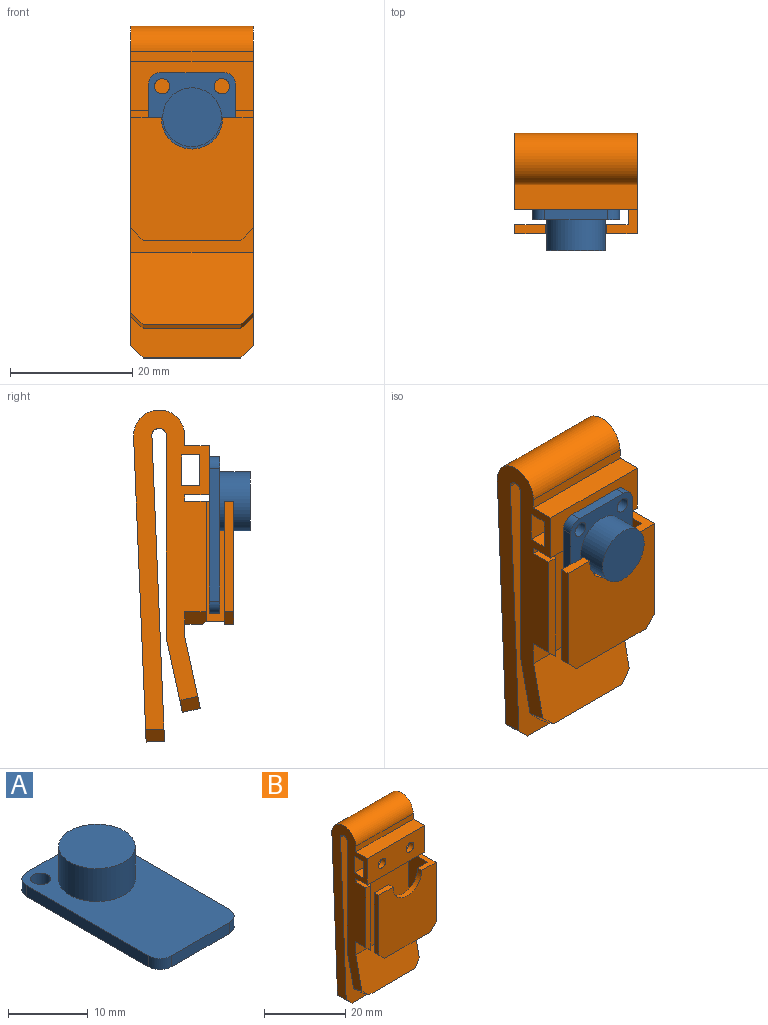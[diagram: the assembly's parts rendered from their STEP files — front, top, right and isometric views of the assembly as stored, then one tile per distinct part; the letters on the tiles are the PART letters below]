
ASSEMBLY  parts=2 mates=1
PART A: 14 faces, bbox 14.3x25.6x6.8 mm
  f0: plane 21.6x1.7mm, normal (1,0,0), area 36.7mm2, adj f1,f9,f10,f11
  f1: cylinder r=2mm len=2mm, axis (0,0,1), area 5.3mm2, adj f0,f2,f10,f11
  f2: plane 10.25x1.7mm, normal (0,1,0), area 17.4mm2, adj f1,f3,f10,f11
  f3: cylinder r=2mm len=2mm, axis (0,0,1), area 5.3mm2, adj f2,f4,f10,f11
  f4: plane 21.6x1.7mm, normal (-1,0,0), area 36.7mm2, adj f3,f5,f10,f11
  f5: cylinder r=2mm len=2mm, axis (0,0,1), area 5.3mm2, adj f4,f6,f10,f11
  f6: plane 10.25x1.7mm, normal (0,-1,0), area 17.4mm2, adj f5,f9,f10,f11
  f7: cylinder r=1.25mm len=2.5mm, axis (0,0,1), area 13.4mm2, adj f10,f11
  f8: cylinder r=1.25mm len=2.5mm, axis (0,0,1), area 13.4mm2, adj f10,f11
  f9: cylinder r=2mm len=2mm, axis (0,0,1), area 5.3mm2, adj f0,f6,f10,f11
  f10: plane 25.6x14.25mm, normal (0,0,-1), area 351.5mm2, adj f0,f1,f2,f3,f4,f5,f6,f7
  f11: plane 25.6x14.25mm, normal (0,0,1), area 279.2mm2, adj f0,f1,f2,f3,f4,f5,f6,f7
  f12: cylinder r=4.8mm len=9.6mm, axis (0,0,-1), area 152.3mm2, adj f11,f13
  f13: plane 9.6x9.6mm, normal (0,0,1), area 72.4mm2, adj f12
PART B: 43 faces, bbox 20x16.4x54.3 mm
  f0: cylinder r=1.35mm len=2.7mm, axis (0,-1,0), area 21.2mm2, adj f11,f40
  f1: cylinder r=1.35mm len=2.7mm, axis (0,-1,0), area 21.2mm2, adj f11,f40
  f2: plane 5x1.5mm, normal (0,0,1), area 7.5mm2, adj f3,f28,f31,f34
  f3: plane 18.04x1.5mm, normal (-1,0,0), area 27.1mm2, adj f2,f31,f34,f37
  f4: plane 16x1.5mm, normal (0,0,-1), area 24mm2, adj f31,f34,f37,f38
  f5: plane 4.59x3.5mm, normal (0,0,1), area 10.7mm2, adj f12,f16,f32,f35
  f6: plane 20x1.67mm, normal (0,-1,0), area 33.3mm2, adj f14,f16,f18,f26
  f7: plane 16x3mm, normal (0,-0.04,-1), area 48mm2, adj f9,f10,f21,f22
  f8: plane 16x2.93mm, normal (0,-0.21,-0.98), area 48mm2, adj f15,f17,f19,f20
  f9: plane 49.96x20mm, normal (0,-1,0.04), area 996.1mm2, adj f7,f13,f16,f18,f21,f22
  f10: plane 50.03x20mm, normal (0,1,-0.04), area 997.5mm2, adj f7,f14,f16,f18,f21,f22
  f11: plane 33.12x20mm, normal (0,1,0), area 651mm2, adj f0,f1,f13,f16,f17,f18
  f12: plane 23.13x20mm, normal (0,-1,0), area 344.4mm2, adj f5,f15,f16,f18,f25,f29,f30,f32
  f13: cylinder r=1.18mm len=20mm, axis (-1,0,0), area 73.6mm2, adj f9,f11,f16,f18
  f14: bspline ~20x8.36mm, area 263.2mm2, adj f6,f10,f16,f18
  f15: plane 20x11.77mm, normal (0,-0.98,0.21), area 237mm2, adj f8,f12,f16,f18,f19,f20
  f16: plane 52.25x12.37mm, normal (-1,0,0), area 378.9mm2, adj f5,f6,f9,f10,f11,f12,f13,f14
  f17: plane 20x12.09mm, normal (0,0.98,-0.21), area 243.5mm2, adj f8,f11,f16,f18,f19,f20
  f18: plane 52.25x16.37mm, normal (1,0,0), area 460.2mm2, adj f6,f9,f10,f11,f12,f13,f14,f15
  f19: plane 3.36x2.59mm, normal (0.71,-0.15,-0.69), area 8.5mm2, adj f8,f15,f17,f18
  f20: plane 3.36x2.59mm, normal (-0.71,-0.15,-0.69), area 8.5mm2, adj f8,f15,f16,f17
  f21: plane 3.08x2.12mm, normal (0.71,-0.03,-0.71), area 8.5mm2, adj f7,f9,f10,f18
  f22: plane 3.08x2.12mm, normal (-0.71,-0.03,-0.71), area 8.5mm2, adj f7,f9,f10,f16
  f23: cylinder r=1.35mm len=2.7mm, axis (0,-1,0), area 12.7mm2, adj f27,f39
  f24: cylinder r=1.35mm len=2.7mm, axis (0,-1,0), area 12.7mm2, adj f27,f39
  f25: plane 20x4mm, normal (0,0,-1), area 80mm2, adj f12,f16,f18,f27
  f26: plane 20x4mm, normal (0,0,1), area 80mm2, adj f6,f16,f18,f27
  f27: plane 20x8mm, normal (0,-1,0), area 148.5mm2, adj f16,f18,f23,f24,f25,f26
  f28: cylinder r=5mm len=10mm, axis (0,1,0), area 24mm2, adj f2,f30,f31,f34
  f29: plane 2.93x2.59mm, normal (0,0,-1), area 3.8mm2, adj f12,f32,f36
  f30: plane 8x5mm, normal (0,0,1), area 17.3mm2, adj f12,f18,f28,f31,f33,f34
  f31: plane 20.04x20mm, normal (0,-1,0), area 355.9mm2, adj f2,f3,f4,f18,f28,f30,f37,f38
  f32: plane 20.04x3.5mm, normal (0.75,-0.66,0), area 93.4mm2, adj f5,f12,f29,f35,f36
  f33: plane 19.54x6.5mm, normal (-1,0,0), area 127mm2, adj f12,f30,f34,f38
  f34: plane 20.04x18.5mm, normal (0,1,0), area 327.7mm2, adj f2,f3,f4,f28,f30,f33,f37,f38
  f35: plane 19.54x1.5mm, normal (0,-1,0), area 28.2mm2, adj f5,f16,f32,f36
  f36: plane 3.5x2mm, normal (-0.71,0,-0.71), area 9.7mm2, adj f12,f16,f29,f32,f35
  f37: plane 2x2mm, normal (-0.71,0,-0.71), area 4.2mm2, adj f3,f4,f31,f34
  f38: plane 8x2mm, normal (0.71,0,-0.71), area 18mm2, adj f4,f12,f18,f31,f33,f34
  f39: plane 20x5mm, normal (0,1,0), area 88.5mm2, adj f16,f18,f23,f24,f41,f42
  f40: plane 20x5mm, normal (0,-1,0), area 88.5mm2, adj f0,f1,f16,f18,f41,f42
  f41: plane 20x3mm, normal (0,0,-1), area 60mm2, adj f16,f18,f39,f40
  f42: plane 20x3mm, normal (0,0,1), area 60mm2, adj f16,f18,f39,f40
PLACE A rot(axis=(1,0,0),90deg) t=(0.01,-14.2,0.47)mm
PLACE B t=(0,-3.7,0)mm
MATE fastened A.f8 <-> B.f0  axis (0,1,0) through (4.88,-12.5,11.03)mm
